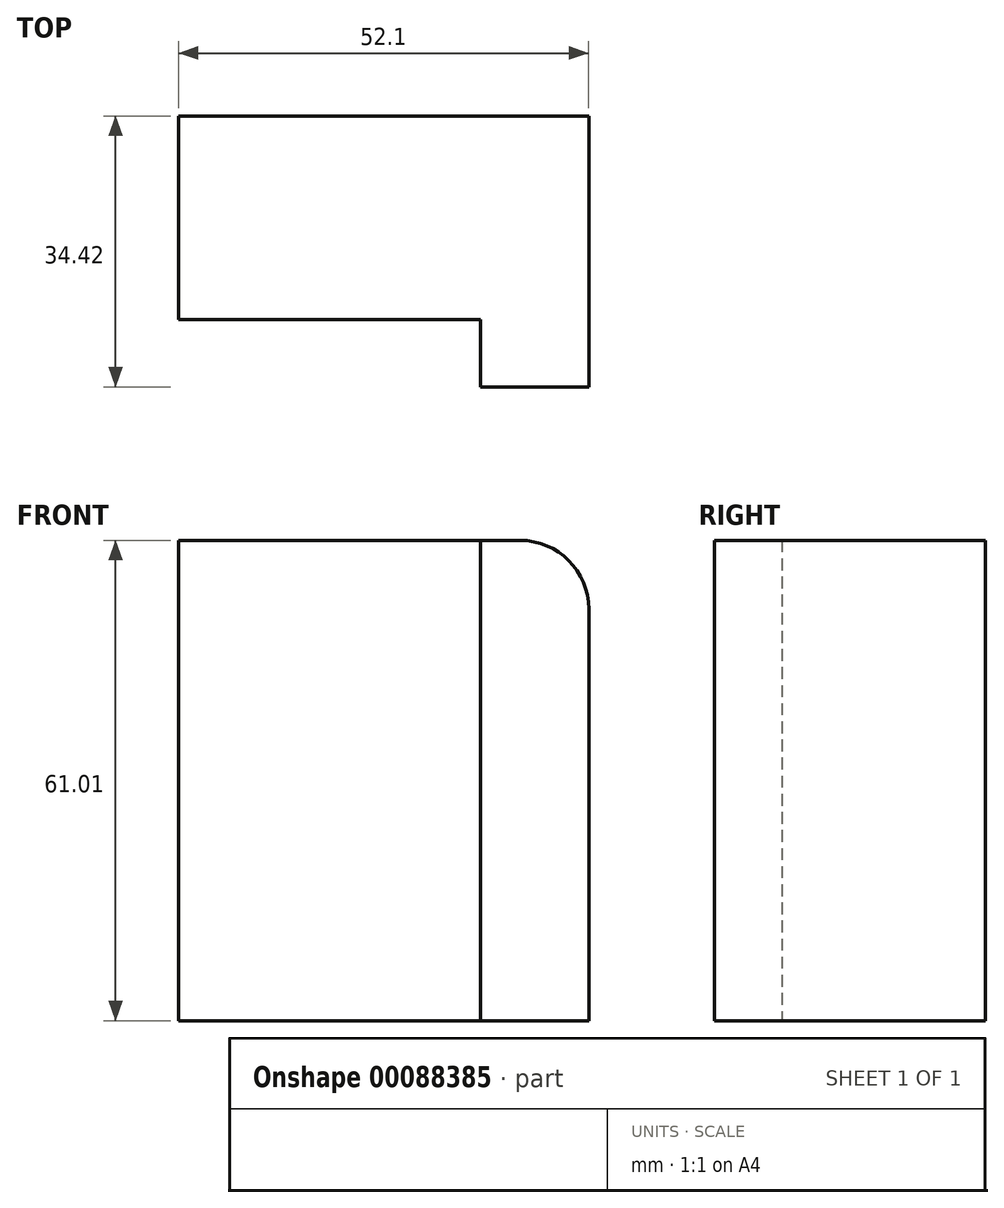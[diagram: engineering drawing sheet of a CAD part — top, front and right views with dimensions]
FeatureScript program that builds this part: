
annotation { "Feature Type Name" : "Feature", "Feature Type Description" : "" }
export const myFeature = defineFeature(function(context is Context, id is Id, definition is map)
    precondition{}
    {
        {
            var Q0;
            Q0=qCreatedBy(makeId("Top.planeOp"),FACE);
            var sketch = newSketch(context, id + "F0", { "sketchPlane" : qUnion([Q0])});
            skLineSegment(sketch, "E0.bottom", {"start": v(-25.5, 30.89) * mm, "end": v(22.51, 30.89) * mm});
            skLineSegment(sketch, "E0.top", {"start": v(-25.5, -5.02) * mm, "end": v(22.51, -5.02) * mm});
            skLineSegment(sketch, "E0.left", {"start": v(-25.5, 30.89) * mm, "end": v(-25.5, -5.02) * mm});
            skLineSegment(sketch, "E0.right", {"start": v(22.51, 30.89) * mm, "end": v(22.51, -5.02) * mm});
            skLineSegment(sketch, "E1.bottom", {"start": v(32, -25.86) * mm, "end": v(-9.68, -25.86) * mm});
            skLineSegment(sketch, "E1.top", {"start": v(32, -14.51) * mm, "end": v(-9.68, -14.51) * mm});
            skLineSegment(sketch, "E1.left", {"start": v(32, -25.86) * mm, "end": v(32, -14.51) * mm});
            skLineSegment(sketch, "E1.right", {"start": v(-9.68, -25.86) * mm, "end": v(-9.68, -14.51) * mm});
            skLineSegment(sketch, "E2.bottom", {"start": v(-15.82, 56.75) * mm, "end": v(36.28, 56.75) * mm});
            skLineSegment(sketch, "E2.top", {"start": v(-15.82, 22.33) * mm, "end": v(36.28, 22.33) * mm});
            skLineSegment(sketch, "E2.left", {"start": v(-15.82, 56.75) * mm, "end": v(-15.82, 22.33) * mm});
            skLineSegment(sketch, "E2.right", {"start": v(36.28, 56.75) * mm, "end": v(36.28, 22.33) * mm});
            skSolve(sketch);
        }
        {
            var Q0;
            {var subQ4=sQuery(id+"F0.wireOp",EDGE,"E2.bottom");Q0=makeQuery(id+"F0.imprint","IMPRINT",FACE,{"disambiguationData":[TD([[makeQuery(id+"F0.imprint","IMPRINT",EDGE,{"derivedFrom":subQ4}),-1.0]])]});}
            extrude(context, id + "F1", {"entities" : qUnion([Q0]), "depth" : 61 * mm});
        }
        {
            var Q0;
            Q0=makeQuery(id+"F1.opExtrude","CAP_EDGE",EDGE,{"disambiguationData":[OSD([sQuery(id+"F0.wireOp",EDGE,"E2.right")])],"isStart":false});
            fillet(context, id + "F2", {"entities" : qUnion([Q0]), "radius" : 8.71 * mm, "tangentPropagation" : true, "allowEdgeOverflow" : false});
        }
    });
